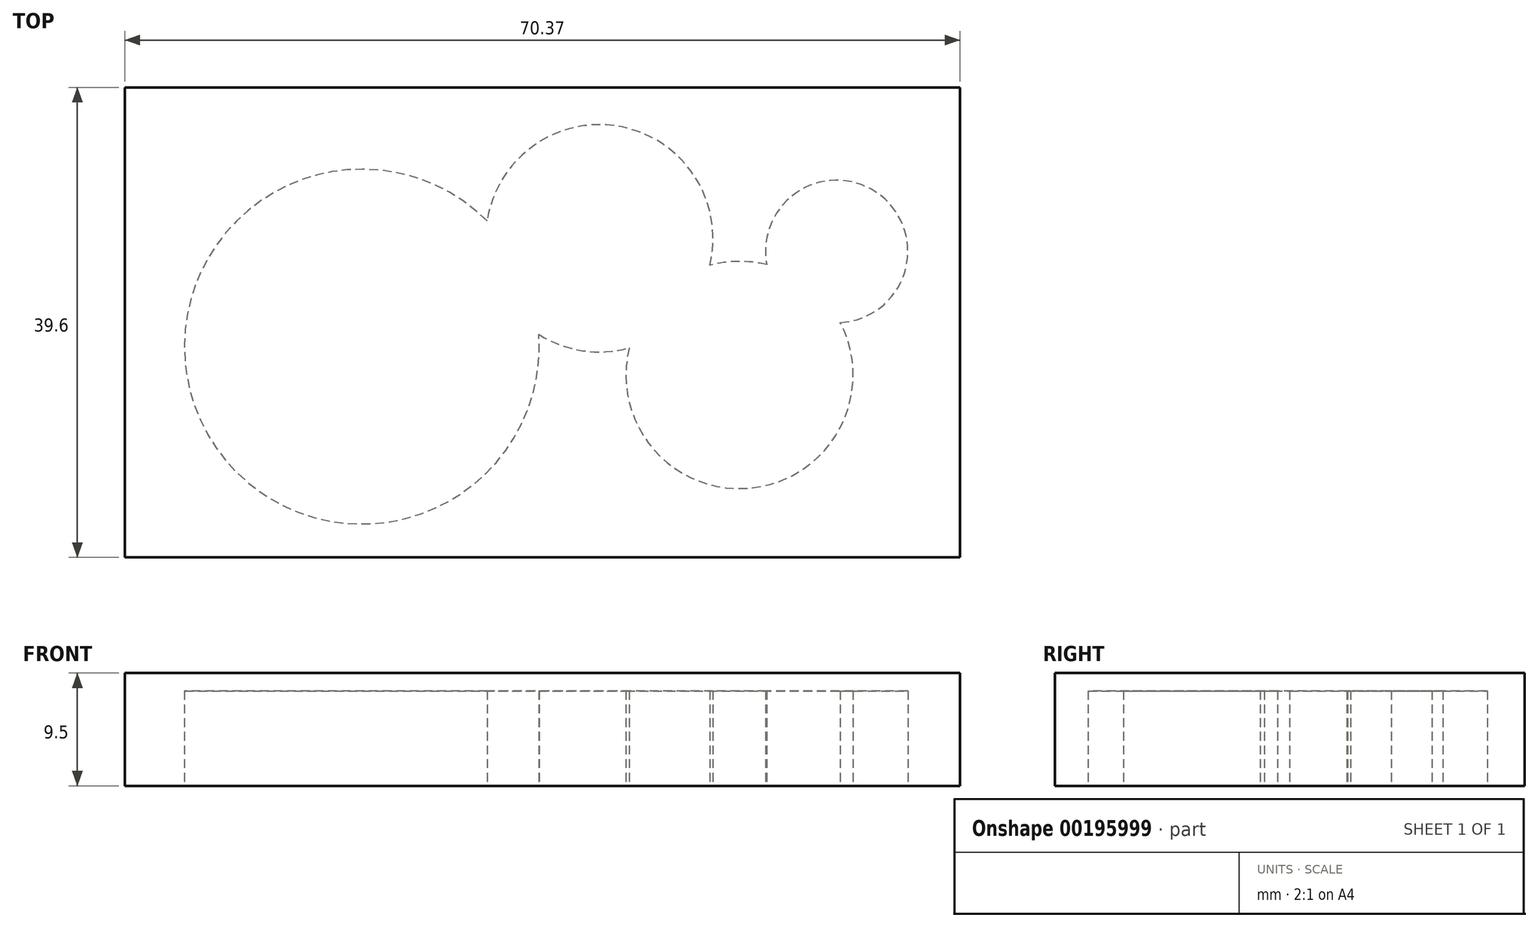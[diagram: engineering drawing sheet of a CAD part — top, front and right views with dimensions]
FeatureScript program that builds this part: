
annotation { "Feature Type Name" : "Feature", "Feature Type Description" : "" }
export const myFeature = defineFeature(function(context is Context, id is Id, definition is map)
    precondition{}
    {
        {
            var Q0;
            Q0=qCreatedBy(makeId("Top.planeOp"),FACE);
            var sketch = newSketch(context, id + "F0", { "sketchPlane" : qUnion([Q0])});
            skLineSegment(sketch, "E0.bottom", {"start": v(-60.93, 6.55) * mm, "end": v(9.44, 6.55) * mm});
            skLineSegment(sketch, "E0.top", {"start": v(-60.93, 46.15) * mm, "end": v(9.44, 46.15) * mm});
            skLineSegment(sketch, "E0.left", {"start": v(-60.93, 6.55) * mm, "end": v(-60.93, 46.15) * mm});
            skLineSegment(sketch, "E0.right", {"start": v(9.44, 6.55) * mm, "end": v(9.44, 46.15) * mm});
            skSolve(sketch);
        }
        {
            var Q0;
            Q0=makeQuery(id+"F0.imprint","IMPRINT",FACE,{"disambiguationData":[TD([[makeQuery(id+"F0.imprint","IMPRINT",EDGE,{"derivedFrom":sQuery(id+"F0.wireOp",EDGE,"E0.bottom")}),1.0]])]});
            var sketch = newSketch(context, id + "F1", { "sketchPlane" : qUnion([Q0])});
            skCircle(sketch, "E1", {"center": v(-20.94, 33.44) * mm, "radius": 2.35 * mm});
            skCircle(sketch, "E2", {"center": v(-9.13, 21.92) * mm, "radius": 9.57 * mm});
            skCircle(sketch, "E3", {"center": v(-20.94, 33.44) * mm, "radius": 9.57 * mm});
            skCircle(sketch, "E4", {"center": v(-0.94, 32.34) * mm, "radius": 6 * mm});
            skCircle(sketch, "E5", {"center": v(-40.96, 24.32) * mm, "radius": 14.95 * mm});
            skSolve(sketch);
        }
        {
            var Q0;
            Q0=makeQuery(id+"F0.imprint","IMPRINT",FACE,{"disambiguationData":[TD([[makeQuery(id+"F0.imprint","IMPRINT",EDGE,{"derivedFrom":sQuery(id+"F0.wireOp",EDGE,"E0.bottom")}),1.0]])]});
            extrude(context, id + "F2", {"entities" : qUnion([Q0]), "depth" : 9.5 * mm});
        }
        {
            var Q0;
            {var subQ0=sQuery(id+"F1.wireOp",EDGE,"E4");var subQ1=sQuery(id+"F1.wireOp",EDGE,"E2");var subQ2=makeQuery(id+"F1.imprint","INTERSECT",VERTEX,{"disambiguationData":[OD(0.0)],"derivedFrom":[subQ1,subQ0]});Q0=makeQuery(id+"F1.imprint","IMPRINT",FACE,{"disambiguationData":[TD([[makeQuery(id+"F1.imprint","IMPRINT",EDGE,{"disambiguationData":[TD([[subQ2,1.0]])],"derivedFrom":subQ1}),-1.0]])]});}
            var Q1;
            {var subQ0=sQuery(id+"F1.wireOp",EDGE,"E3");var subQ1=sQuery(id+"F1.wireOp",EDGE,"E2");var subQ2=makeQuery(id+"F1.imprint","INTERSECT",VERTEX,{"disambiguationData":[OD(0.0)],"derivedFrom":[subQ1,subQ0]});Q1=makeQuery(id+"F1.imprint","IMPRINT",FACE,{"disambiguationData":[TD([[makeQuery(id+"F1.imprint","IMPRINT",EDGE,{"disambiguationData":[TD([[subQ2,-1.0]])],"derivedFrom":subQ1}),1.0]])]});}
            var Q2;
            {var subQ0=sQuery(id+"F1.wireOp",EDGE,"E4");var subQ1=sQuery(id+"F1.wireOp",EDGE,"E2");var subQ2=makeQuery(id+"F1.imprint","INTERSECT",VERTEX,{"disambiguationData":[OD(0.0)],"derivedFrom":[subQ1,subQ0]});Q2=makeQuery(id+"F1.imprint","IMPRINT",FACE,{"disambiguationData":[TD([[makeQuery(id+"F1.imprint","IMPRINT",EDGE,{"disambiguationData":[TD([[subQ2,1.0]])],"derivedFrom":subQ1}),1.0]])]});}
            var Q3;
            {var subQ0=sQuery(id+"F1.wireOp",EDGE,"E4");var subQ1=sQuery(id+"F1.wireOp",EDGE,"E2");var subQ2=makeQuery(id+"F1.imprint","INTERSECT",VERTEX,{"disambiguationData":[OD(0.0)],"derivedFrom":[subQ1,subQ0]});Q3=makeQuery(id+"F1.imprint","IMPRINT",FACE,{"disambiguationData":[TD([[makeQuery(id+"F1.imprint","IMPRINT",EDGE,{"disambiguationData":[TD([[subQ2,-1.0]])],"derivedFrom":subQ1}),1.0]])]});}
            var Q4;
            Q4=makeQuery(id+"F1.imprint","IMPRINT",FACE,{"disambiguationData":[TD([[makeQuery(id+"F1.imprint","IMPRINT",EDGE,{"derivedFrom":sQuery(id+"F1.wireOp",EDGE,"E1")}),-1.0]])]});
            var Q5;
            Q5=makeQuery(id+"F1.imprint","IMPRINT",FACE,{"disambiguationData":[TD([[makeQuery(id+"F1.imprint","IMPRINT",EDGE,{"derivedFrom":sQuery(id+"F1.wireOp",EDGE,"E1")}),1.0]])]});
            var Q6;
            {var subQ0=sQuery(id+"F1.wireOp",EDGE,"E5");var subQ1=sQuery(id+"F1.wireOp",EDGE,"E3");var subQ2=makeQuery(id+"F1.imprint","INTERSECT",VERTEX,{"disambiguationData":[OD(0.0)],"derivedFrom":[subQ1,subQ0]});Q6=makeQuery(id+"F1.imprint","IMPRINT",FACE,{"disambiguationData":[TD([[makeQuery(id+"F1.imprint","IMPRINT",EDGE,{"disambiguationData":[TD([[subQ2,1.0]])],"derivedFrom":subQ1}),-1.0]])]});}
            var Q7;
            {var subQ0=sQuery(id+"F1.wireOp",EDGE,"E5");var subQ1=sQuery(id+"F1.wireOp",EDGE,"E3");var subQ2=makeQuery(id+"F1.imprint","INTERSECT",VERTEX,{"disambiguationData":[OD(0.0)],"derivedFrom":[subQ1,subQ0]});Q7=makeQuery(id+"F1.imprint","IMPRINT",FACE,{"disambiguationData":[TD([[makeQuery(id+"F1.imprint","IMPRINT",EDGE,{"disambiguationData":[TD([[subQ2,1.0]])],"derivedFrom":subQ1}),1.0]])]});}
            extrude(context, id + "F3", {"entities" : qUnion([Q0, Q1, Q2, Q3, Q4, Q5, Q6, Q7]), "operationType" : NewBodyOperationType.REMOVE, "depth" : 8 * mm});
        }
        {
            var Q0;
            Q0=makeQuery(id+"F3.boolean.opBoolean","COPY",FACE,{"derivedFrom":makeQuery(id+"F3.opExtrude","CAP_FACE",FACE,{"disambiguationData":[OSD([sQuery(id+"F1.wireOp",EDGE,"E2"),sQuery(id+"F1.wireOp",EDGE,"E3"),sQuery(id+"F1.wireOp",EDGE,"E4"),sQuery(id+"F1.wireOp",EDGE,"E5")])],"isStart":false})});
            var sketch = newSketch(context, id + "F4", { "sketchPlane" : qUnion([Q0])});
            skCircle(sketch, "E6", {"center": v(-20.94, -33.44) * mm, "radius": 2.43 * mm});
            skCircle(sketch, "E7", {"center": v(-9.13, -21.92) * mm, "radius": 2.43 * mm});
            skCircle(sketch, "E8", {"center": v(-9.13, -21.92) * mm, "radius": 3.75 * mm});
            skCircle(sketch, "E9", {"center": v(-20.94, -33.44) * mm, "radius": 3.75 * mm});
            skSolve(sketch);
        }
        {
            var Q0;
            Q0=sQuery(id+"F4.wireOp",EDGE,"E8");
            var Q1;
            Q1=sQuery(id+"F4.wireOp",EDGE,"E9");
            extrude(context, id + "F5", {"bodyType" : ToolBodyType.SURFACE, "surfaceEntities" : qUnion([Q0, Q1]), "depth" : 2 * mm});
        }
    });
